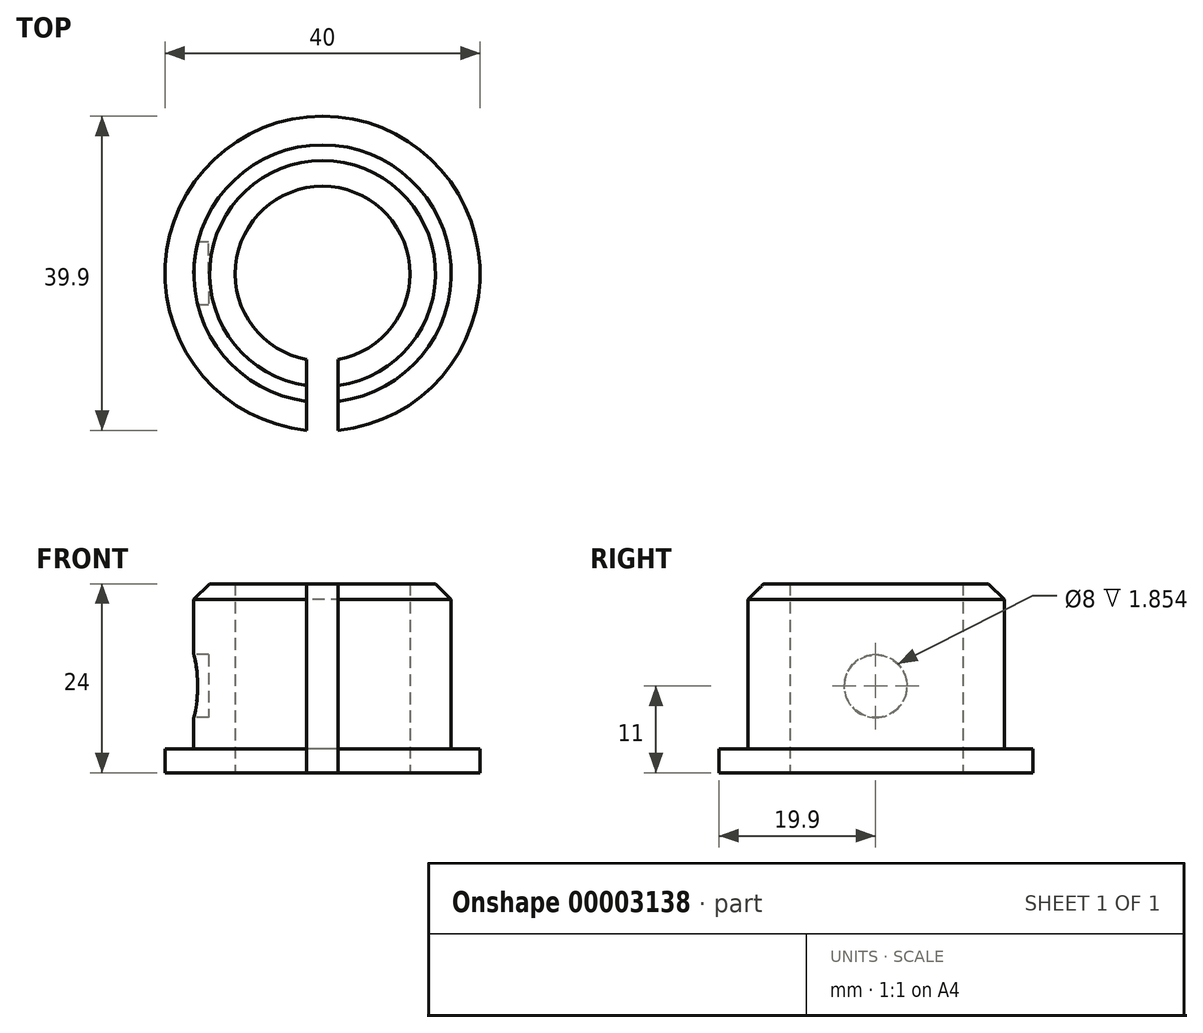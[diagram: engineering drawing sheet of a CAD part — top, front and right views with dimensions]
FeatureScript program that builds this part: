
annotation { "Feature Type Name" : "Feature", "Feature Type Description" : "" }
export const myFeature = defineFeature(function(context is Context, id is Id, definition is map)
    precondition{}
    {
        {
            var Q0;
            Q0=qCreatedBy(makeId("Top.planeOp"),FACE);
            var sketch = newSketch(context, id + "F0", { "sketchPlane" : qUnion([Q0])});
            skCircle(sketch, "E0", {"center": v(0, 0) * mm, "radius": 16.35 * mm});
            skCircle(sketch, "E1", {"center": v(0, 0) * mm, "radius": 11.1 * mm});
            skCircle(sketch, "E2", {"center": v(0, 0) * mm, "radius": 20 * mm});
            skSolve(sketch);
        }
        {
            var Q0;
            Q0=makeQuery(id+"F0.imprint","IMPRINT",FACE,{"disambiguationData":[TD([[makeQuery(id+"F0.imprint","IMPRINT",EDGE,{"derivedFrom":sQuery(id+"F0.wireOp",EDGE,"E0")}),1.0]])]});
            extrude(context, id + "F1", {"entities" : qUnion([Q0]), "depth" : 24 * mm});
        }
        {
            var Q0;
            Q0=makeQuery(id+"F0.imprint","IMPRINT",FACE,{"disambiguationData":[TD([[makeQuery(id+"F0.imprint","IMPRINT",EDGE,{"derivedFrom":sQuery(id+"F0.wireOp",EDGE,"E0")}),-1.0]])]});
            extrude(context, id + "F2", {"entities" : qUnion([Q0]), "operationType" : NewBodyOperationType.ADD, "depth" : 3 * mm});
        }
        {
            var Q0;
            Q0=makeQuery(id+"F1.opExtrude","CAP_EDGE",EDGE,{"disambiguationData":[OSD([sQuery(id+"F0.wireOp",EDGE,"E0")])],"isStart":false});
            chamfer(context, id + "F3", {"entities" : qUnion([Q0]), "width" : 2 * mm, "tangentPropagation" : true});
        }
        {
            var Q0;
            Q0=makeQuery(id+"F0.imprint","IMPRINT",FACE,{"disambiguationData":[TD([[makeQuery(id+"F0.imprint","IMPRINT",EDGE,{"derivedFrom":sQuery(id+"F0.wireOp",EDGE,"E1")}),1.0]])]});
            var sketch = newSketch(context, id + "F4", { "sketchPlane" : qUnion([Q0])});
            skLineSegment(sketch, "E3.bottom", {"start": v(0, 0) * mm, "end": v(2, 0) * mm});
            skLineSegment(sketch, "E3.top", {"start": v(0, -21.54) * mm, "end": v(2, -21.54) * mm});
            skLineSegment(sketch, "E3.left", {"start": v(0, 0) * mm, "end": v(0, -21.54) * mm});
            skLineSegment(sketch, "E3.right", {"start": v(2, 0) * mm, "end": v(2, -21.54) * mm});
            skLineSegment(sketch, "E4.bottom", {"start": v(0, 0) * mm, "end": v(-2, 0) * mm});
            skLineSegment(sketch, "E4.top", {"start": v(0, -21.79) * mm, "end": v(-2, -21.79) * mm});
            skLineSegment(sketch, "E4.left", {"start": v(0, 0) * mm, "end": v(0, -21.79) * mm});
            skLineSegment(sketch, "E4.right", {"start": v(-2, 0) * mm, "end": v(-2, -21.79) * mm});
            skSolve(sketch);
        }
        {
            var Q0;
            Q0 = qSketchRegion(id + "F4", true);
            extrude(context, id + "F5", {"entities" : qUnion([Q0]), "operationType" : NewBodyOperationType.REMOVE, "depth" : 25 * mm});
        }
        {
            var Q0;
            Q0=qCreatedBy(makeId("Right.planeOp"),FACE);
            var sketch = newSketch(context, id + "F6", { "sketchPlane" : qUnion([Q0])});
            skCircle(sketch, "E5", {"center": v(0, 11) * mm, "radius": 4 * mm});
            skSolve(sketch);
        }
        {
            var Q0;
            Q0=makeQuery(id+"F6.imprint","IMPRINT",FACE,{"disambiguationData":[TD([[makeQuery(id+"F6.imprint","IMPRINT",EDGE,{"derivedFrom":sQuery(id+"F6.wireOp",EDGE,"E5")}),1.0]])]});
            extrude(context, id + "F7", {"entities" : qUnion([Q0]), "operationType" : NewBodyOperationType.ADD, "oppositeDirection" : true, "depth" : 20 * mm});
        }
        {
            var Q0;
            Q0=makeQuery(id+"F7.opExtrude","CAP_FACE",FACE,{"disambiguationData":[OSD([sQuery(id+"F6.wireOp",EDGE,"E5")])],"isStart":false});
            extrude(context, id + "F8", {"entities" : qUnion([Q0]), "operationType" : NewBodyOperationType.REMOVE, "oppositeDirection" : true, "depth" : 5.5 * mm});
        }
        {
            var Q0;
            Q0=makeQuery(id+"F1.opExtrude","CAP_FACE",FACE,{"disambiguationData":[OSD([sQuery(id+"F0.wireOp",EDGE,"E0"),sQuery(id+"F0.wireOp",EDGE,"E1")])],"isStart":false});
            var sketch = newSketch(context, id + "F9", { "sketchPlane" : qUnion([Q0])});
            skCircle(sketch, "E6", {"center": v(0, 0) * mm, "radius": 11.1 * mm});
            skSolve(sketch);
        }
        {
            var Q0;
            Q0 = qSketchRegion(id + "F9", true);
            extrude(context, id + "F10", {"entities" : qUnion([Q0]), "operationType" : NewBodyOperationType.REMOVE, "oppositeDirection" : true, "depth" : 25 * mm});
        }
    });
